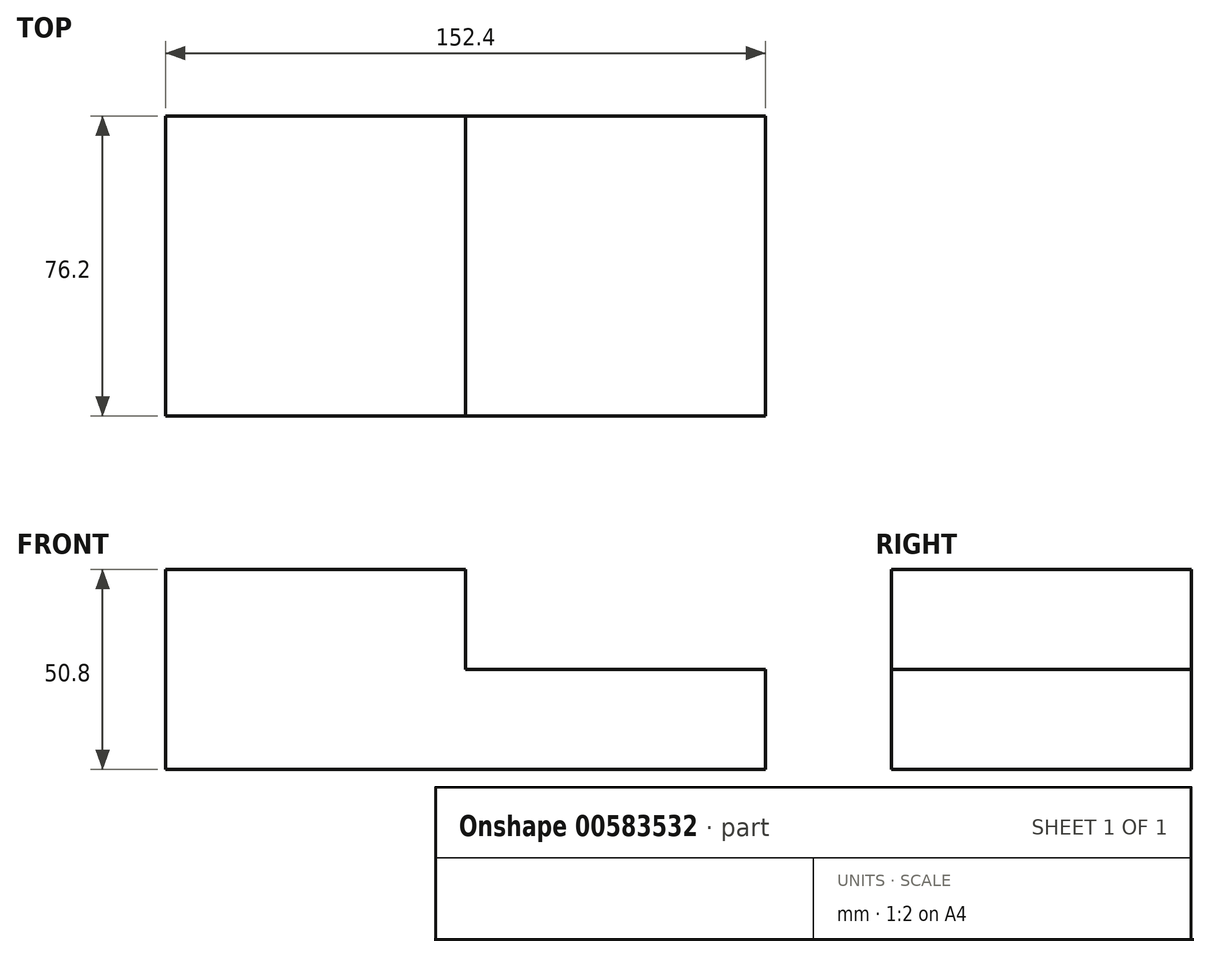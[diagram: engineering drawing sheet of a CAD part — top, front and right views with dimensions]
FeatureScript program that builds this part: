
annotation { "Feature Type Name" : "Feature", "Feature Type Description" : "" }
export const myFeature = defineFeature(function(context is Context, id is Id, definition is map)
    precondition{}
    {
        {
            var Q0;
            Q0=qCreatedBy(makeId("Front.planeOp"),FACE);
            var sketch = newSketch(context, id + "F0", { "sketchPlane" : qUnion([Q0])});
            skLineSegment(sketch, "E0", {"start": v(0, 0) * mm, "end": v(0, 50.8) * mm});
            skLineSegment(sketch, "E1", {"start": v(0, 50.8) * mm, "end": v(76.2, 50.8) * mm});
            skLineSegment(sketch, "E2", {"start": v(76.2, 50.8) * mm, "end": v(76.2, 25.4) * mm});
            skLineSegment(sketch, "E3", {"start": v(76.2, 25.4) * mm, "end": v(152.4, 25.4) * mm});
            skLineSegment(sketch, "E4", {"start": v(152.4, 25.4) * mm, "end": v(152.4, 0) * mm});
            skLineSegment(sketch, "E5", {"start": v(0, 0) * mm, "end": v(152.4, 0) * mm});
            skSolve(sketch);
        }
        {
            var Q0;
            Q0 = qSketchRegion(id + "F0", true);
            extrude(context, id + "F1", {"entities" : qUnion([Q0]), "depth" : 76.2 * mm, "offsetDistance" : 25.4 * mm});
        }
    });
